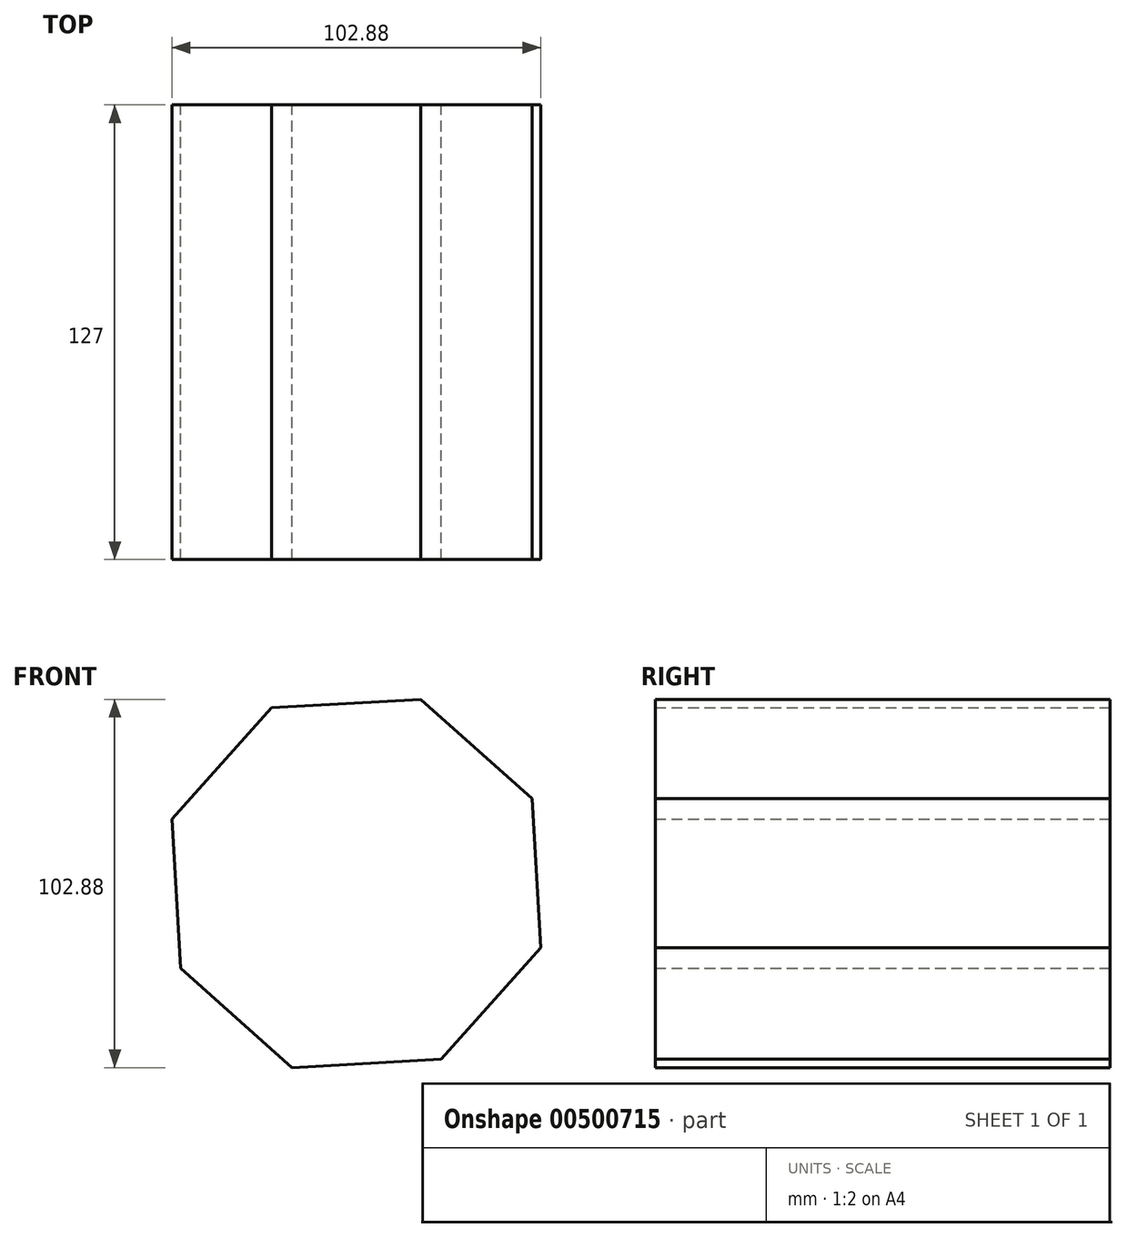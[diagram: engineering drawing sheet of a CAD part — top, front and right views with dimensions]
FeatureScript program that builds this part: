
annotation { "Feature Type Name" : "Feature", "Feature Type Description" : "" }
export const myFeature = defineFeature(function(context is Context, id is Id, definition is map)
    precondition{}
    {
        {
            var Q0;
            Q0=qCreatedBy(makeId("Front.planeOp"),FACE);
            var sketch = newSketch(context, id + "F0", { "sketchPlane" : qUnion([Q0])});
            skCircle(sketch, "E0.cCircle", {"center": v(0, 0) * mm, "radius": 54.49 * mm, "construction": true});
            skLineSegment(sketch, "E0.0", {"start": v(49.08, 23.67) * mm, "end": v(51.44, -17.97) * mm});
            skLineSegment(sketch, "E0.1", {"start": v(51.44, -17.97) * mm, "end": v(23.67, -49.08) * mm});
            skLineSegment(sketch, "E0.2", {"start": v(23.67, -49.08) * mm, "end": v(-17.97, -51.44) * mm});
            skLineSegment(sketch, "E0.3", {"start": v(-17.97, -51.44) * mm, "end": v(-49.08, -23.67) * mm});
            skLineSegment(sketch, "E0.4", {"start": v(-49.08, -23.67) * mm, "end": v(-51.44, 17.97) * mm});
            skLineSegment(sketch, "E0.5", {"start": v(-51.44, 17.97) * mm, "end": v(-23.67, 49.08) * mm});
            skLineSegment(sketch, "E0.6", {"start": v(-23.67, 49.08) * mm, "end": v(17.97, 51.44) * mm});
            skLineSegment(sketch, "E0.7", {"start": v(17.97, 51.44) * mm, "end": v(49.08, 23.67) * mm});
            skSolve(sketch);
        }
        {
            var Q0;
            Q0=makeQuery(id+"F0.imprint","IMPRINT",FACE,{"disambiguationData":[TD([[makeQuery(id+"F0.imprint","IMPRINT",EDGE,{"derivedFrom":sQuery(id+"F0.wireOp",EDGE,"E0.0")}),-1.0]])]});
            extrude(context, id + "F1", {"entities" : qUnion([Q0]), "depth" : 127 * mm});
        }
    });
